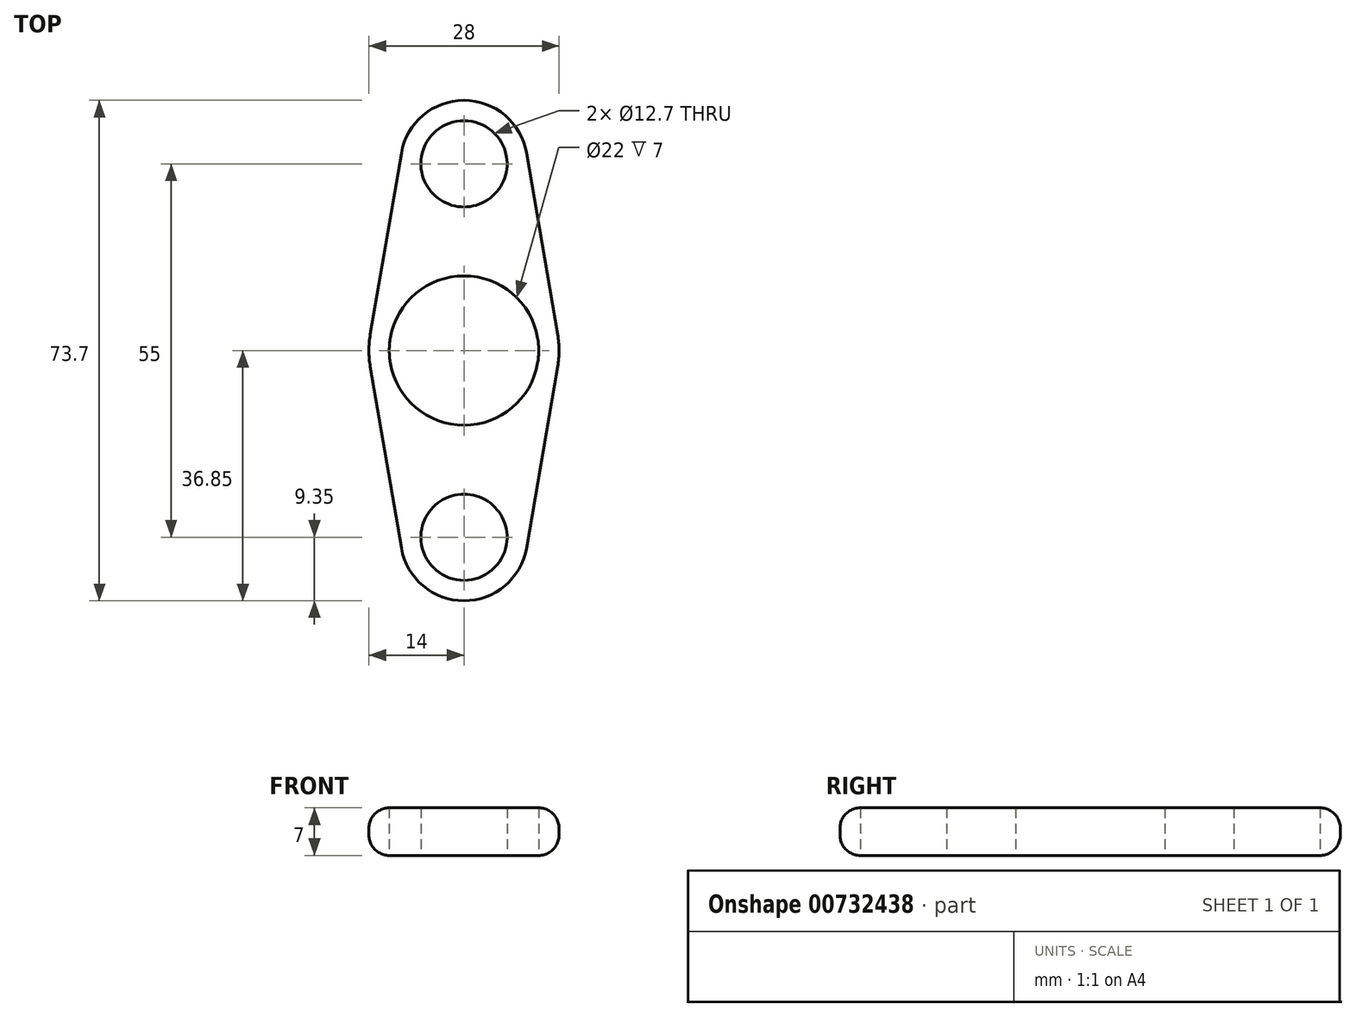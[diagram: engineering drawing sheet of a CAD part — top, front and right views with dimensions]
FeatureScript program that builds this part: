
annotation { "Feature Type Name" : "Feature", "Feature Type Description" : "" }
export const myFeature = defineFeature(function(context is Context, id is Id, definition is map)
    precondition{}
    {
        {
            var Q0;
            Q0=qCreatedBy(makeId("Top.planeOp"),FACE);
            var sketch = newSketch(context, id + "F0", { "sketchPlane" : qUnion([Q0])});
            skCircle(sketch, "E0", {"center": v(0, 0) * mm, "radius": 11 * mm});
            skCircle(sketch, "E1", {"center": v(0, 0) * mm, "radius": 27.5 * mm, "construction": true});
            skCircle(sketch, "E2", {"center": v(0, 27.5) * mm, "radius": 6.35 * mm});
            skArc(sketch, "E3.0", {"start": v(9.22, 29.08) * mm, "mid": v(0, 36.85) * mm, "end": v(-9.22, 29.08) * mm});
            skArc(sketch, "E4.0", {"start": v(-13.8, 2.37) * mm, "mid": v(-14, 0) * mm, "end": v(-13.8, -2.37) * mm});
            skLineSegment(sketch, "E5", {"start": v(-9.22, 29.08) * mm, "end": v(-13.8, 2.37) * mm});
            skLineSegment(sketch, "E6.MirrorCS", {"start": v(9.22, 29.08) * mm, "end": v(13.8, 2.37) * mm});
            skLineSegment(sketch, "E7.MirrorCS", {"start": v(-9.22, -29.08) * mm, "end": v(-13.8, -2.37) * mm});
            skLineSegment(sketch, "E8.MirrorCS", {"start": v(9.22, -29.08) * mm, "end": v(13.8, -2.37) * mm});
            skArc(sketch, "E9.MirrorCS", {"start": v(9.22, -29.08) * mm, "mid": v(0, -36.85) * mm, "end": v(-9.22, -29.08) * mm});
            skCircle(sketch, "E10.MirrorC", {"center": v(0, -27.5) * mm, "radius": 6.35 * mm});
            skArc(sketch, "E11.trimOffspring", {"start": v(13.8, -2.37) * mm, "mid": v(14, 0) * mm, "end": v(13.8, 2.37) * mm});
            skSolve(sketch);
        }
        {
            var Q0;
            Q0=makeQuery(id+"F0.imprint","IMPRINT",FACE,{"disambiguationData":[TD([[makeQuery(id+"F0.imprint","IMPRINT",EDGE,{"derivedFrom":sQuery(id+"F0.wireOp",EDGE,"E0")}),-1.0]])]});
            extrude(context, id + "F1", {"entities" : qUnion([Q0]), "depth" : 7 * mm, "offsetDistance" : 25 * mm});
        }
        {
            var Q0;
            Q0=makeQuery(id+"F1.opExtrude","CAP_EDGE",EDGE,{"disambiguationData":[OSD([sQuery(id+"F0.wireOp",EDGE,"E8.MirrorCS")])],"isStart":false});
            var Q1;
            Q1=makeQuery(id+"F1.opExtrude","CAP_EDGE",EDGE,{"disambiguationData":[OSD([sQuery(id+"F0.wireOp",EDGE,"E8.MirrorCS")])],"isStart":true});
            fillet(context, id + "F2", {"entities" : qUnion([Q0, Q1]), "radius" : 3 * mm, "tangentPropagation" : true, "allowEdgeOverflow" : false});
        }
    });
